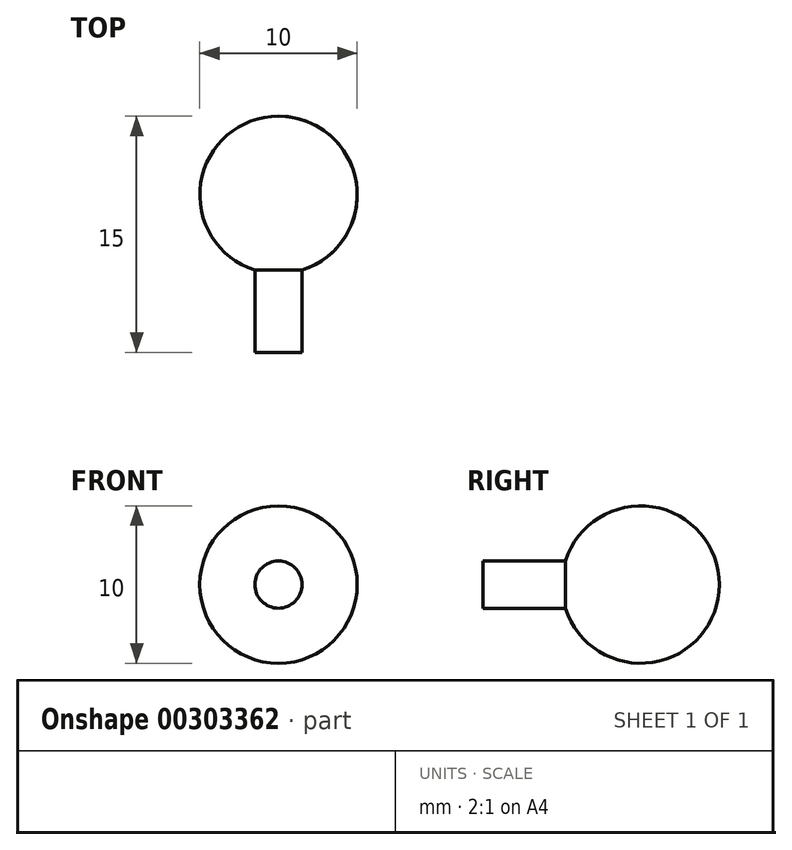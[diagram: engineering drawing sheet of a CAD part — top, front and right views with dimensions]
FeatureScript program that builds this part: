
annotation { "Feature Type Name" : "Feature", "Feature Type Description" : "" }
export const myFeature = defineFeature(function(context is Context, id is Id, definition is map)
    precondition{}
    {
        {
            var Q0;
            Q0=qCreatedBy(makeId("Top.planeOp"),FACE);
            var sketch = newSketch(context, id + "F0", { "sketchPlane" : qUnion([Q0])});
            skArc(sketch, "E0", {"start": v(1.5, -4.77) * mm, "mid": v(4.94, 0.76) * mm, "end": v(0, 5) * mm});
            skLineSegment(sketch, "E1.top", {"start": v(-1.5, -10) * mm, "end": v(1.5, -10) * mm});
            skLineSegment(sketch, "E1.right", {"start": v(1.5, -4.77) * mm, "end": v(1.5, -10) * mm});
            skPoint(sketch, "E2.orphan", {"position": v(-1.5, 0) * mm});
            skLineSegment(sketch, "E3", {"start": v(0, 5) * mm, "end": v(0, -11.02) * mm});
            skPoint(sketch, "E3.endSnap0", {"position": v(0, -10) * mm});
            skSolve(sketch);
        }
        {
            var Q0;
            Q0 = qSketchRegion(id + "F0", true);
            var Q1;
            Q1=sQuery(id+"F0.wireOp",EDGE,"E3");
            revolve(context, id + "F1", {"entities" : qUnion([Q0]), "axis" : qUnion([Q1]), "revolveType" : RevolveType.FULL});
        }
    });
